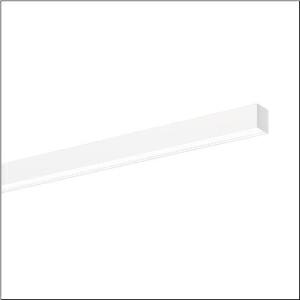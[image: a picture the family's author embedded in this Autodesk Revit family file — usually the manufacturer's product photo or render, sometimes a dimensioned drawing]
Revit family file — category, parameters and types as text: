
# Revit family: silica_r__21_51mx20tat2w_a418
name_source: partatom
category: Lighting Fixtures
units: mm (PartAtom-declared; Revit-internal decimal feet)

## family parameters
Cut with Voids When Loaded = No
Host = Face
Light Source = No
Part Type = Normal
Room Calculation Point = No
Round Connector Dimension = Use Diameter
Shared = No

## types (1)
- --- (1 x LED, 2400 lm, 20.5 W, 6500K)
    Apparent Load = 21 VA
    CIE Flux Codes = 48 79 96 100 100
    Color Rendering = 80
    Color Temperature = 6500K
    Default Elevation = 1800 mm
    Description = Silica® 21, office luminaire, primary optical cover: cover, of PMMA, opal, light emission: direct distribution, primary light characteristic: symmetric, installation type: surface-mounted, LED, rated luminous flux: 2.400lm, luminous efficacy: 112lm/W, light colour: 8tw, colour temperature: 2700..6500K, control gear: ECG DALI, with terminal, 3+2-pole, max. 2.5mm², mains connection: 220..240V, AC, 50/60Hz, rated input power: 21.5W, luminaire housing, of aluminium, traffic white (RAL 9016), length: 1.204mm, width: 53mm, height: 53mm, protection rating (complete): IP20, insulation class (complete): insulation class I (protective earthing), certification: CE, permissible operating ambient temperature: 0..+35°C, standard: EN 50419, packaging unit: 1 piece
    Height = 0 mm  [stored 0 ft]
    Lamp = 1 x LED
    Lamp Light Flux = 2400 lm
    Lamp Power = 20.5 W
    Lamp count = 1
    Length = 1204 mm
    Luminous efficacy = 117 lm/W
    Manufacturer = Siteco
    ModVariant = No
    Model = 51MX20TAT2W
    Mounting Place = Ceiling
    Mounting Type = Recessed
    Number of Poles = 1
    OnlyDefault = Yes
    Power Factor = 1
    Product Name = Silica® 21
    Product group = office luminaire | ceiling recessed
    ProductGroupID = 401
    Protection Class = Protection class I
    Protection Degree = IP 20
    RLX_Detail_Level = 1
    RLX_Emergency_Light_Flux = 0 lm
    RLX_Emergency_Type = 0
    RLX_Emergency_Type_DB = No
    RlxData = <blob elided: 20733 chars, md5=f73ec32f>
    Socket = socket
    Standby Power = 0 W
    System Light Flux = 2400 lm
    System Power = 21 W
    Type Comments = individual setting
    Type Image = l_1313601.jpg
    URL = http://relux.com
    VarID = @adj_089079
    Voltage = 0 V
    Weight = 0.00 kg
    Width = 53 mm

note: [stored X ft] marks values corroborated as IEEE doubles in the binary element streams (Revit-internal decimal feet)

## geometry (parser evidence)
native form markers: Blend x4, Sweep x13
no freeform markers — native parametric forms only
